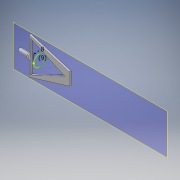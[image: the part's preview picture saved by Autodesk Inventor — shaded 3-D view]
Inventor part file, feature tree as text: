
AUTODESK INVENTOR PART (.ipt)
format: ipt  version: 2018 (Build 220112000, 112)  size: 206,336 bytes
history: native  units: mm
features: sketch x11, extrude x10, plane x1, projected_geometry x1
ambient origin geometry x8: Origin, YZ Plane, XZ Plane, XY Plane, X Axis, Y Axis, Z Axis, Center Point
bodies: Solid1 (feature_tree)
feature tree (23):
  extrude  "Extrusion1"  Depth=10.0mm TaperAngle=0.0deg
  sketch  "Sketch2"  dims[d3=9.0mm d4=8.0mm d5=10.0mm d6=0.0mm]
  extrude  "Extrusion2"  Depth=10.0mm TaperAngle=0.0deg
  extrude  "Extrusion3"  Depth=1.125mm
  extrude  "Extrusion4"  Depth=1.6mm
  extrude  "Extrusion5"  Depth=1.8mm
  extrude  "Extrusion6"  Depth=2.4mm
  extrude  "Extrusion7"  Depth=3.32mm
  extrude  "Extrusion8"  Depth=10.0mm
  extrude  "Extrusion9"  Depth=15.0mm TaperAngle=0.0deg
  plane  "Work Plane1"
  extrude  "Extrusion11"  Depth=1.175mm
  sketch  "Sketch1"  dims[d0=10.0mm d1=10.0mm d2=0.0mm]
  sketch  "Sketch3"  dims[d9=1.125mm d10=1.125mm]
  sketch  "Sketch4"  dims[d12=0.0mm d13=0.0mm d16=1.6mm]
  sketch  "Sketch5"  dims[d18=1.6mm d21=1.8mm]
  projected_geometry  "Projected Loop1"
  sketch  "Sketch6"  dims[d23=1.8mm d24=2.4mm]
  sketch  "Sketch7"  dims[d26=3.32mm d27=3.32mm]
  sketch  "Sketch8"  dims[d29=10.0mm d30=0.0mm d31=5.0mm]
  sketch  "Sketch9"  dims[d32=2.4mm d33=15.0mm d34=0.0mm]
  sketch  "Sketch10"  dims[d35=15.0mm d36=0.0mm d37=1.175mm]
  sketch  "Sketch12"  dims[d38=7.0mm d39=0.0mm d40=10.0mm d41=0.0mm d42=8.0mm d43=0.0mm d60=4.1mm d61=25.4mm d62=29.4mm d63=14.7mm d64=10.0mm d65=1.5mm d66=0.0mm d67=31.0mm d69=2.5mm]
